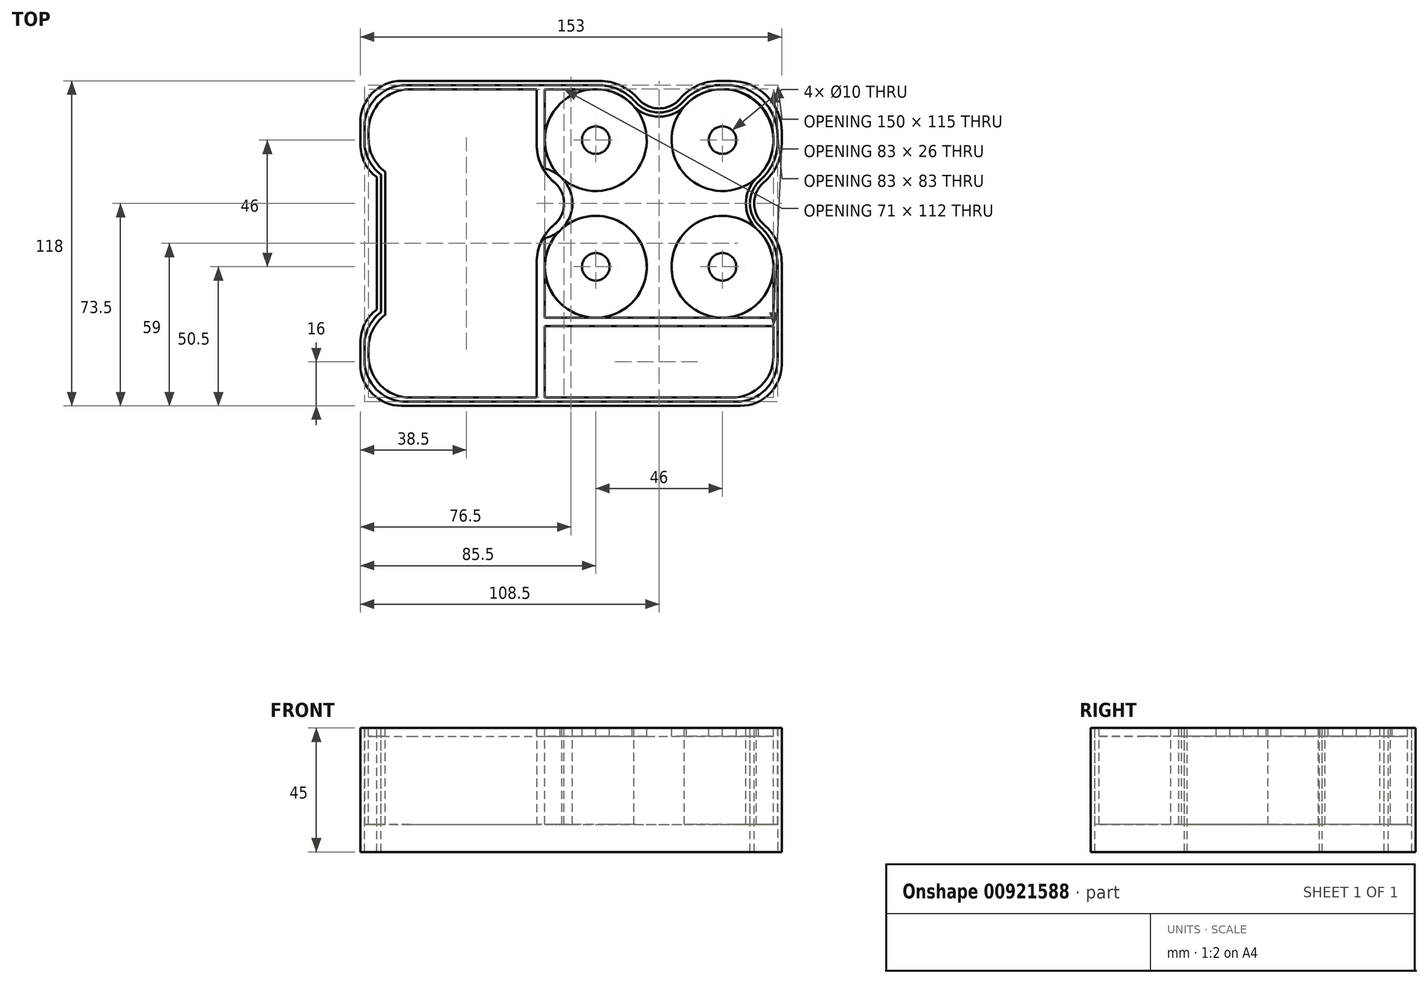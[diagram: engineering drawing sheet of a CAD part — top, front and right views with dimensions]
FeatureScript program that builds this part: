
annotation { "Feature Type Name" : "Feature", "Feature Type Description" : "" }
export const myFeature = defineFeature(function(context is Context, id is Id, definition is map)
    precondition{}
    {
        {
            var Q0;
            Q0=qCreatedBy(makeId("Top.planeOp"),FACE);
            var sketch = newSketch(context, id + "F0", { "sketchPlane" : qUnion([Q0])});
            skLineSegment(sketch, "E0.bottom", {"start": v(-44.5, 44.5) * mm, "end": v(-10, 44.5) * mm});
            skLineSegment(sketch, "E0.top", {"start": v(-44.5, -44.5) * mm, "end": v(41.5, -44.5) * mm});
            skLineSegment(sketch, "E0.left", {"start": v(-44.5, 41.5) * mm, "end": v(-44.5, 10) * mm});
            skLineSegment(sketch, "E0.right", {"start": v(44.5, 44.5) * mm, "end": v(44.5, 10) * mm});
            skPoint(sketch, "E0.middle", {"position": v(0, 0) * mm});
            skArc(sketch, "E1", {"start": v(-44.5, -10) * mm, "mid": v(-34.5, 0) * mm, "end": v(-44.5, 10) * mm});
            skArc(sketch, "E2", {"start": v(44.5, 10) * mm, "mid": v(34.5, 0) * mm, "end": v(44.5, -10) * mm});
            skArc(sketch, "E3", {"start": v(-10, 44.5) * mm, "mid": v(0, 34.5) * mm, "end": v(10, 44.5) * mm});
            skLineSegment(sketch, "E4.trimOffspring", {"start": v(10, 44.5) * mm, "end": v(44.5, 44.5) * mm});
            skLineSegment(sketch, "E5.trimOffspring", {"start": v(44.5, -10) * mm, "end": v(44.5, -44.5) * mm});
            skLineSegment(sketch, "E6.trimOffspring", {"start": v(-44.5, -10) * mm, "end": v(-44.5, -44.5) * mm});
            skLineSegment(sketch, "E7.bottom", {"start": v(-43, 43) * mm, "end": v(-11.4, 43) * mm});
            skLineSegment(sketch, "E7.top", {"start": v(-43, -43) * mm, "end": v(41.5, -43) * mm});
            skLineSegment(sketch, "E7.left", {"start": v(-43, 41.5) * mm, "end": v(-43, 11.4) * mm});
            skLineSegment(sketch, "E7.right", {"start": v(43, 43) * mm, "end": v(43, 11.4) * mm});
            skArc(sketch, "E8", {"start": v(-43, -11.4) * mm, "mid": v(-33, 0) * mm, "end": v(-43, 11.4) * mm});
            skArc(sketch, "E9", {"start": v(43, 11.4) * mm, "mid": v(33, 0) * mm, "end": v(43, -11.4) * mm});
            skArc(sketch, "E10", {"start": v(-11.4, 43) * mm, "mid": v(0, 33) * mm, "end": v(11.4, 43) * mm});
            skLineSegment(sketch, "E11.trimOffspring", {"start": v(-43, -11.4) * mm, "end": v(-43, -43) * mm});
            skLineSegment(sketch, "E12.trimOffspring", {"start": v(11.4, 43) * mm, "end": v(43, 43) * mm});
            skLineSegment(sketch, "E13.trimOffspring", {"start": v(43, -11.4) * mm, "end": v(43, -43) * mm});
            skLineSegment(sketch, "E14.bottom", {"start": v(-41.5, 41.5) * mm, "end": v(-12.65, 41.5) * mm});
            skLineSegment(sketch, "E14.top", {"start": v(-41.5, -41.5) * mm, "end": v(41.5, -41.5) * mm});
            skLineSegment(sketch, "E14.left", {"start": v(-41.5, 41.5) * mm, "end": v(-41.5, 12.65) * mm});
            skLineSegment(sketch, "E14.right", {"start": v(41.5, 41.5) * mm, "end": v(41.5, 12.65) * mm});
            skArc(sketch, "E15", {"start": v(-41.5, -12.65) * mm, "mid": v(-31.5, 0) * mm, "end": v(-41.5, 12.65) * mm});
            skArc(sketch, "E16", {"start": v(41.5, 12.65) * mm, "mid": v(31.5, 0) * mm, "end": v(41.5, -12.65) * mm});
            skArc(sketch, "E17", {"start": v(-12.65, 41.5) * mm, "mid": v(0, 31.5) * mm, "end": v(12.65, 41.5) * mm});
            skLineSegment(sketch, "E18.trimOffspring", {"start": v(12.65, 41.5) * mm, "end": v(41.5, 41.5) * mm});
            skLineSegment(sketch, "E19.trimOffspring", {"start": v(41.5, -12.65) * mm, "end": v(41.5, -41.5) * mm});
            skLineSegment(sketch, "E20.trimOffspring", {"start": v(-41.5, -12.65) * mm, "end": v(-41.5, -41.5) * mm});
            skLineSegment(sketch, "E21.bottom", {"start": v(-23, 23) * mm, "end": v(23, 23) * mm, "construction": true});
            skLineSegment(sketch, "E21.top", {"start": v(-23, -23) * mm, "end": v(23, -23) * mm, "construction": true});
            skLineSegment(sketch, "E21.left", {"start": v(-23, 23) * mm, "end": v(-23, -23) * mm, "construction": true});
            skLineSegment(sketch, "E21.right", {"start": v(23, 23) * mm, "end": v(23, -23) * mm, "construction": true});
            skCircle(sketch, "E22", {"center": v(-23, 23) * mm, "radius": 18.5 * mm});
            skCircle(sketch, "E23", {"center": v(23, 23) * mm, "radius": 18.5 * mm});
            skCircle(sketch, "E24", {"center": v(23, -23) * mm, "radius": 18.5 * mm});
            skCircle(sketch, "E25", {"center": v(-23, -23) * mm, "radius": 18.5 * mm});
            skLineSegment(sketch, "E26.top", {"start": v(44.5, -73.5) * mm, "end": v(-44.5, -73.5) * mm});
            skLineSegment(sketch, "E26.left", {"start": v(44.5, -44.5) * mm, "end": v(44.5, -73.5) * mm});
            skLineSegment(sketch, "E26.right", {"start": v(-44.5, -44.5) * mm, "end": v(-44.5, -73.5) * mm});
            skPoint(sketch, "E26.middle", {"position": v(0, -59) * mm});
            skLineSegment(sketch, "E27.bottom", {"start": v(-43, -72) * mm, "end": v(43, -72) * mm});
            skLineSegment(sketch, "E27.left", {"start": v(-43, -70.5) * mm, "end": v(-43, -46) * mm});
            skLineSegment(sketch, "E27.right", {"start": v(43, -72) * mm, "end": v(43, -46) * mm});
            skLineSegment(sketch, "E28.top", {"start": v(-41.5, -70.5) * mm, "end": v(41.5, -70.5) * mm});
            skLineSegment(sketch, "E28.left", {"start": v(-41.5, -47.5) * mm, "end": v(-41.5, -70.5) * mm});
            skLineSegment(sketch, "E28.right", {"start": v(41.5, -47.5) * mm, "end": v(41.5, -70.5) * mm});
            skLineSegment(sketch, "E29.bottom", {"start": v(-44.5, -73.5) * mm, "end": v(-108.5, -73.5) * mm});
            skLineSegment(sketch, "E29.top", {"start": v(-44, 44.5) * mm, "end": v(-108.5, 44.5) * mm});
            skLineSegment(sketch, "E29.left", {"start": v(-44.5, -73.5) * mm, "end": v(-44.5, 41.5) * mm});
            skLineSegment(sketch, "E29.right", {"start": v(-108.5, -73.5) * mm, "end": v(-108.5, -38.5) * mm});
            skLineSegment(sketch, "E30", {"start": v(-108.5, -14.5) * mm, "end": v(-44.5, -14.5) * mm, "construction": true});
            skPoint(sketch, "E31", {"position": v(-76.5, -14.5) * mm});
            skLineSegment(sketch, "E32.bottom", {"start": v(-107, 43) * mm, "end": v(-46, 43) * mm});
            skLineSegment(sketch, "E32.top", {"start": v(-107, -72) * mm, "end": v(-46, -72) * mm});
            skLineSegment(sketch, "E32.left", {"start": v(-107, 43) * mm, "end": v(-107, 10.5) * mm});
            skLineSegment(sketch, "E32.right", {"start": v(-46, 41.5) * mm, "end": v(-46, -70.5) * mm});
            skLineSegment(sketch, "E33.bottom", {"start": v(-105.5, 41.5) * mm, "end": v(-47.5, 41.5) * mm});
            skLineSegment(sketch, "E33.top", {"start": v(-105.5, -70.5) * mm, "end": v(-47.5, -70.5) * mm});
            skLineSegment(sketch, "E33.left", {"start": v(-105.5, 41.5) * mm, "end": v(-105.5, 11.5) * mm});
            skLineSegment(sketch, "E33.right", {"start": v(-47.5, 41.5) * mm, "end": v(-47.5, -70.5) * mm});
            skLineSegment(sketch, "E34", {"start": v(41.5, -41.5) * mm, "end": v(41.5, -47.5) * mm});
            skLineSegment(sketch, "E35", {"start": v(43, -43) * mm, "end": v(43, -46) * mm});
            skLineSegment(sketch, "E36.trimOffspring", {"start": v(41.5, -44.5) * mm, "end": v(-44.5, -44.5) * mm});
            skLineSegment(sketch, "E37", {"start": v(-47.5, -70.5) * mm, "end": v(-41.5, -70.5) * mm});
            skLineSegment(sketch, "E38", {"start": v(-46, -72) * mm, "end": v(-43, -72) * mm});
            skLineSegment(sketch, "E39", {"start": v(-46, 43) * mm, "end": v(-43, 43) * mm});
            skLineSegment(sketch, "E40", {"start": v(-47.5, 41.5) * mm, "end": v(-41.5, 41.5) * mm});
            skLineSegment(sketch, "E41", {"start": v(-43, -46) * mm, "end": v(-43, -44.5) * mm});
            skLineSegment(sketch, "E42", {"start": v(-41.5, -47.5) * mm, "end": v(-41.5, -45) * mm});
            skLineSegment(sketch, "E43", {"start": v(-41.5, -45) * mm, "end": v(-41.5, -44.5) * mm});
            skCircle(sketch, "E44", {"center": v(-23, 23) * mm, "radius": 5 * mm});
            skCircle(sketch, "E45", {"center": v(23, 23) * mm, "radius": 5 * mm});
            skCircle(sketch, "E46", {"center": v(-23, -23) * mm, "radius": 5 * mm});
            skCircle(sketch, "E47", {"center": v(23, -23) * mm, "radius": 5 * mm});
            skLineSegment(sketch, "E48", {"start": v(-102.5, 9.5) * mm, "end": v(-102.5, -37.89) * mm});
            skLineSegment(sketch, "E49", {"start": v(-101, -37.89) * mm, "end": v(-101, 10.5) * mm});
            skLineSegment(sketch, "E50", {"start": v(-99.5, -37.89) * mm, "end": v(-99.5, 9.5) * mm});
            skLineSegment(sketch, "E51", {"start": v(-102.5, 9.5) * mm, "end": v(-108.5, 9.5) * mm});
            skLineSegment(sketch, "E52", {"start": v(-107, 10.5) * mm, "end": v(-101, 10.5) * mm});
            skLineSegment(sketch, "E53", {"start": v(-99.5, 9.5) * mm, "end": v(-99.5, 10.5) * mm});
            skLineSegment(sketch, "E54", {"start": v(-105.5, 11.5) * mm, "end": v(-99.5, 11.5) * mm});
            skLineSegment(sketch, "E55", {"start": v(-99.5, 11.5) * mm, "end": v(-99.5, 10.5) * mm});
            skLineSegment(sketch, "E56", {"start": v(-108.5, -38.5) * mm, "end": v(-102.5, -38.5) * mm});
            skLineSegment(sketch, "E57", {"start": v(-102.5, -38.5) * mm, "end": v(-102.5, -37.89) * mm});
            skLineSegment(sketch, "E58", {"start": v(-107, -39.5) * mm, "end": v(-101, -39.5) * mm});
            skLineSegment(sketch, "E59", {"start": v(-101, -39.5) * mm, "end": v(-101, -37.89) * mm});
            skLineSegment(sketch, "E60", {"start": v(-105.5, -40.5) * mm, "end": v(-99.5, -40.5) * mm});
            skLineSegment(sketch, "E61", {"start": v(-99.5, -40.5) * mm, "end": v(-99.5, -37.89) * mm});
            skLineSegment(sketch, "E62.trimOffspring", {"start": v(-107, -39.5) * mm, "end": v(-107, -72) * mm});
            skLineSegment(sketch, "E63.trimOffspring", {"start": v(-105.5, -40.5) * mm, "end": v(-105.5, -70.5) * mm});
            skLineSegment(sketch, "E64.trimOffspring", {"start": v(-108.5, 9.5) * mm, "end": v(-108.5, 44.5) * mm});
            skSolve(sketch);
        }
        {
            var Q0;
            Q0=makeQuery(id+"F0.imprint","IMPRINT",FACE,{"disambiguationData":[TD([[makeQuery(id+"F0.imprint","IMPRINT",EDGE,{"derivedFrom":sQuery(id+"F0.wireOp",EDGE,"E14.bottom")}),-1.0]])]});
            var Q1;
            {var subQ5=sQuery(id+"F0.wireOp",EDGE,"E15");Q1=makeQuery(id+"F0.imprint","IMPRINT",FACE,{"disambiguationData":[TD([[makeQuery(id+"F0.imprint","IMPRINT",EDGE,{"derivedFrom":subQ5}),-1.0]])]});}
            var Q2;
            {var subQ0=sQuery(id+"F0.wireOp",EDGE,"E20.trimOffspring");var subQ1=sQuery(id+"F0.wireOp",EDGE,"E14.top");var subQ2=makeQuery(id+"F0.imprint","INTERSECT",VERTEX,{"derivedFrom":[subQ1,subQ0]});Q2=makeQuery(id+"F0.imprint","IMPRINT",FACE,{"disambiguationData":[TD([[makeQuery(id+"F0.imprint","IMPRINT",EDGE,{"disambiguationData":[TD([[subQ2,-1.0]])],"derivedFrom":subQ1}),1.0]])]});}
            var Q3;
            {var subQ0=sQuery(id+"F0.wireOp",EDGE,"E25");var subQ1=sQuery(id+"F0.wireOp",EDGE,"E14.top");var subQ2=makeQuery(id+"F0.imprint","INTERSECT",VERTEX,{"derivedFrom":[subQ1,subQ0]});Q3=makeQuery(id+"F0.imprint","IMPRINT",FACE,{"disambiguationData":[TD([[makeQuery(id+"F0.imprint","IMPRINT",EDGE,{"disambiguationData":[TD([[subQ2,-1.0]])],"derivedFrom":subQ1}),1.0]])]});}
            var Q4;
            {var subQ0=sQuery(id+"F0.wireOp",EDGE,"E19.trimOffspring");var subQ1=sQuery(id+"F0.wireOp",EDGE,"E14.top");var subQ2=makeQuery(id+"F0.imprint","INTERSECT",VERTEX,{"derivedFrom":[subQ1,subQ0]});Q4=makeQuery(id+"F0.imprint","IMPRINT",FACE,{"disambiguationData":[TD([[makeQuery(id+"F0.imprint","IMPRINT",EDGE,{"disambiguationData":[TD([[subQ2,1.0]])],"derivedFrom":subQ1}),1.0]])]});}
            var Q5;
            {var subQ1=sQuery(id+"F0.wireOp",EDGE,"E16");Q5=makeQuery(id+"F0.imprint","IMPRINT",FACE,{"disambiguationData":[TD([[makeQuery(id+"F0.imprint","IMPRINT",EDGE,{"derivedFrom":subQ1}),-1.0]])]});}
            var Q6;
            {var subQ0=sQuery(id+"F0.wireOp",EDGE,"E18.trimOffspring");var subQ1=sQuery(id+"F0.wireOp",EDGE,"E14.right");var subQ2=makeQuery(id+"F0.imprint","INTERSECT",VERTEX,{"derivedFrom":[subQ1,subQ0]});Q6=makeQuery(id+"F0.imprint","IMPRINT",FACE,{"disambiguationData":[TD([[makeQuery(id+"F0.imprint","IMPRINT",EDGE,{"disambiguationData":[TD([[subQ2,-1.0]])],"derivedFrom":subQ1}),-1.0]])]});}
            var Q7;
            {var subQ8=sQuery(id+"F0.wireOp",EDGE,"E17");Q7=makeQuery(id+"F0.imprint","IMPRINT",FACE,{"disambiguationData":[TD([[makeQuery(id+"F0.imprint","IMPRINT",EDGE,{"derivedFrom":subQ8}),-1.0]])]});}
            var Q8;
            {var subQ7=sQuery(id+"F0.wireOp",EDGE,"E22");var subQ12=sQuery(id+"F0.wireOp",EDGE,"E21.bottom");var subQ15=makeQuery(id+"F0.imprint","INTERSECT",VERTEX,{"derivedFrom":[subQ12,subQ7]});Q8=makeQuery(id+"F0.imprint","IMPRINT",FACE,{"disambiguationData":[TD([[makeQuery(id+"F0.imprint","IMPRINT",EDGE,{"disambiguationData":[TD([[subQ15,-1.0]])],"derivedFrom":subQ12}),-1.0]])]});}
            var Q9;
            Q9=makeQuery(id+"F0.imprint","IMPRINT",FACE,{"disambiguationData":[TD([[makeQuery(id+"F0.imprint","IMPRINT",EDGE,{"derivedFrom":sQuery(id+"F0.wireOp",EDGE,"E33.bottom")}),-1.0]])]});
            var Q10;
            Q10=makeQuery(id+"F0.imprint","IMPRINT",FACE,{"disambiguationData":[TD([[makeQuery(id+"F0.imprint","IMPRINT",EDGE,{"derivedFrom":sQuery(id+"F0.wireOp",EDGE,"E28.bottom")}),-1.0]])]});
            var Q11;
            {var subQ0=sQuery(id+"F0.wireOp",EDGE,"E32.right");Q11=makeQuery(id+"F0.imprint","IMPRINT",FACE,{"disambiguationData":[TD([[makeQuery(id+"F0.imprint","IMPRINT",EDGE,{"derivedFrom":subQ0}),-1.0]])]});}
            var Q12;
            {var subQ0=sQuery(id+"F0.wireOp",EDGE,"E1");Q12=makeQuery(id+"F0.imprint","IMPRINT",FACE,{"disambiguationData":[TD([[makeQuery(id+"F0.imprint","IMPRINT",EDGE,{"derivedFrom":subQ0}),1.0]])]});}
            var Q13;
            {var subQ9=sQuery(id+"F0.wireOp",EDGE,"E32.right");Q13=makeQuery(id+"F0.imprint","IMPRINT",FACE,{"disambiguationData":[TD([[makeQuery(id+"F0.imprint","IMPRINT",EDGE,{"derivedFrom":subQ9}),1.0]])]});}
            var Q14;
            Q14=makeQuery(id+"F0.imprint","IMPRINT",FACE,{"disambiguationData":[TD([[makeQuery(id+"F0.imprint","IMPRINT",EDGE,{"derivedFrom":sQuery(id+"F0.wireOp",EDGE,"E28.top")}),1.0]])]});
            extrude(context, id + "F1", {"entities" : qUnion([Q0, Q1, Q2, Q3, Q4, Q5, Q6, Q7, Q8, Q9, Q10, Q11, Q12, Q13, Q14]), "oppositeDirection" : true, "depth" : 3 * mm, "offsetDistance" : 25 * mm});
        }
        {
            var Q0;
            Q0=makeQuery(id+"F0.imprint","IMPRINT",FACE,{"disambiguationData":[TD([[makeQuery(id+"F0.imprint","IMPRINT",EDGE,{"derivedFrom":sQuery(id+"F0.wireOp",EDGE,"E0.bottom")}),-1.0]])]});
            extrude(context, id + "F2", {"entities" : qUnion([Q0]), "oppositeDirection" : true, "depth" : 45 * mm, "offsetDistance" : 25 * mm});
        }
        {
            var Q0;
            Q0=makeQuery(id+"F0.imprint","IMPRINT",FACE,{"disambiguationData":[TD([[makeQuery(id+"F0.imprint","IMPRINT",EDGE,{"derivedFrom":sQuery(id+"F0.wireOp",EDGE,"E7.bottom")}),-1.0]])]});
            var Q1;
            {var subQ9=sQuery(id+"F0.wireOp",EDGE,"E32.top");Q1=makeQuery(id+"F0.imprint","IMPRINT",FACE,{"disambiguationData":[TD([[makeQuery(id+"F0.imprint","IMPRINT",EDGE,{"derivedFrom":subQ9}),1.0]])]});}
            var Q2;
            {var subQ5=sQuery(id+"F0.wireOp",EDGE,"E1");Q2=makeQuery(id+"F0.imprint","IMPRINT",FACE,{"disambiguationData":[TD([[makeQuery(id+"F0.imprint","IMPRINT",EDGE,{"derivedFrom":subQ5}),-1.0]])]});}
            var Q3;
            {var subQ7=sQuery(id+"F0.wireOp",EDGE,"E7.top");Q3=makeQuery(id+"F0.imprint","IMPRINT",FACE,{"disambiguationData":[TD([[makeQuery(id+"F0.imprint","IMPRINT",EDGE,{"derivedFrom":subQ7}),1.0]])]});}
            var Q4;
            {var subQ6=sQuery(id+"F0.wireOp",EDGE,"E27.left");Q4=makeQuery(id+"F0.imprint","IMPRINT",FACE,{"disambiguationData":[TD([[makeQuery(id+"F0.imprint","IMPRINT",EDGE,{"derivedFrom":subQ6}),1.0]])]});}
            var Q5;
            {var subQ1=sQuery(id+"F0.wireOp",EDGE,"E27.left");Q5=makeQuery(id+"F0.imprint","IMPRINT",FACE,{"disambiguationData":[TD([[makeQuery(id+"F0.imprint","IMPRINT",EDGE,{"derivedFrom":subQ1}),-1.0]])]});}
            extrude(context, id + "F3", {"entities" : qUnion([Q0, Q1, Q2, Q3, Q4, Q5]), "oppositeDirection" : true, "depth" : 35 * mm, "offsetDistance" : 25 * mm});
        }
        {
            var Q0;
            Q0=makeQuery(id+"F0.imprint","IMPRINT",FACE,{"disambiguationData":[TD([[makeQuery(id+"F0.imprint","IMPRINT",EDGE,{"derivedFrom":sQuery(id+"F0.wireOp",EDGE,"E44")}),1.0]])]});
            var Q1;
            Q1=makeQuery(id+"F0.imprint","IMPRINT",FACE,{"disambiguationData":[TD([[makeQuery(id+"F0.imprint","IMPRINT",EDGE,{"derivedFrom":sQuery(id+"F0.wireOp",EDGE,"E45")}),1.0]])]});
            var Q2;
            Q2=makeQuery(id+"F0.imprint","IMPRINT",FACE,{"disambiguationData":[TD([[makeQuery(id+"F0.imprint","IMPRINT",EDGE,{"derivedFrom":sQuery(id+"F0.wireOp",EDGE,"E47")}),1.0]])]});
            var Q3;
            Q3=makeQuery(id+"F0.imprint","IMPRINT",FACE,{"disambiguationData":[TD([[makeQuery(id+"F0.imprint","IMPRINT",EDGE,{"derivedFrom":sQuery(id+"F0.wireOp",EDGE,"E46")}),1.0]])]});
            extrude(context, id + "F4", {"entities" : qUnion([Q0, Q1, Q2, Q3]), "oppositeDirection" : true, "depth" : 3 * mm, "offsetDistance" : 25 * mm});
        }
        {
            var Q0;
            Q0=makeQuery(id+"F0.imprint","IMPRINT",FACE,{"disambiguationData":[TD([[makeQuery(id+"F0.imprint","IMPRINT",EDGE,{"derivedFrom":sQuery(id+"F0.wireOp",EDGE,"E44")}),-1.0]])]});
            var Q1;
            Q1=makeQuery(id+"F0.imprint","IMPRINT",FACE,{"disambiguationData":[TD([[makeQuery(id+"F0.imprint","IMPRINT",EDGE,{"derivedFrom":sQuery(id+"F0.wireOp",EDGE,"E45")}),-1.0]])]});
            var Q2;
            Q2=makeQuery(id+"F0.imprint","IMPRINT",FACE,{"disambiguationData":[TD([[makeQuery(id+"F0.imprint","IMPRINT",EDGE,{"derivedFrom":sQuery(id+"F0.wireOp",EDGE,"E46")}),-1.0]])]});
            var Q3;
            Q3=makeQuery(id+"F0.imprint","IMPRINT",FACE,{"disambiguationData":[TD([[makeQuery(id+"F0.imprint","IMPRINT",EDGE,{"derivedFrom":sQuery(id+"F0.wireOp",EDGE,"E47")}),-1.0]])]});
            extrude(context, id + "F5", {"entities" : qUnion([Q0, Q1, Q2, Q3]), "oppositeDirection" : true, "depth" : 3 * mm, "offsetDistance" : 25 * mm});
        }
        {
            var Q0;
            Q0=makeQuery(id+"F2.opExtrude","SWEPT_EDGE",EDGE,{"disambiguationData":[OSD([sQuery(id+"F0.wireOp",EDGE,"E0.right"),sQuery(id+"F0.wireOp",EDGE,"E4.trimOffspring")])]});
            var Q1;
            Q1=makeQuery(id+"F2.opExtrude","SWEPT_EDGE",EDGE,{"disambiguationData":[OSD([sQuery(id+"F0.wireOp",EDGE,"E7.right"),sQuery(id+"F0.wireOp",EDGE,"E12.trimOffspring")])]});
            var Q2;
            Q2=makeQuery(id+"F2.opExtrude","SWEPT_EDGE",EDGE,{"disambiguationData":[OSD([sQuery(id+"F0.wireOp",EDGE,"E0.right"),sQuery(id+"F0.wireOp",EDGE,"E2")])]});
            var Q3;
            Q3=makeQuery(id+"F2.opExtrude","SWEPT_EDGE",EDGE,{"disambiguationData":[OSD([sQuery(id+"F0.wireOp",EDGE,"E7.right"),sQuery(id+"F0.wireOp",EDGE,"E9")])]});
            var Q4;
            Q4=makeQuery(id+"F2.opExtrude","SWEPT_EDGE",EDGE,{"disambiguationData":[OSD([sQuery(id+"F0.wireOp",EDGE,"E3"),sQuery(id+"F0.wireOp",EDGE,"E4.trimOffspring")])]});
            var Q5;
            Q5=makeQuery(id+"F2.opExtrude","SWEPT_EDGE",EDGE,{"disambiguationData":[OSD([sQuery(id+"F0.wireOp",EDGE,"E10"),sQuery(id+"F0.wireOp",EDGE,"E12.trimOffspring")])]});
            var Q6;
            Q6=makeQuery(id+"F2.opExtrude","SWEPT_EDGE",EDGE,{"disambiguationData":[OSD([sQuery(id+"F0.wireOp",EDGE,"E0.bottom"),sQuery(id+"F0.wireOp",EDGE,"E3")])]});
            var Q7;
            Q7=makeQuery(id+"F2.opExtrude","SWEPT_EDGE",EDGE,{"disambiguationData":[OSD([sQuery(id+"F0.wireOp",EDGE,"E7.bottom"),sQuery(id+"F0.wireOp",EDGE,"E10")])]});
            var Q8;
            Q8=makeQuery(id+"F2.opExtrude","SWEPT_EDGE",EDGE,{"disambiguationData":[OSD([sQuery(id+"F0.wireOp",EDGE,"E2"),sQuery(id+"F0.wireOp",EDGE,"E5.trimOffspring")])]});
            var Q9;
            Q9=makeQuery(id+"F2.opExtrude","SWEPT_EDGE",EDGE,{"disambiguationData":[OSD([sQuery(id+"F0.wireOp",EDGE,"E9"),sQuery(id+"F0.wireOp",EDGE,"E13.trimOffspring")])]});
            var Q10;
            {var subQ0=sQuery(id+"F0.wireOp",EDGE,"E29.left");var subQ1=sQuery(id+"F0.wireOp",EDGE,"E1");Q10=makeQuery(id+"FE6vsyq0CEjp5Nf_9.opExtrude","SWEPT_EDGE",EDGE,{"disambiguationData":[OSD([subQ1,subQ0]),TDD([makeQuery(id+"F0.imprint","INTERSECT",VERTEX,{"disambiguationData":[OD(1.0)],"derivedFrom":[subQ1,subQ0]})])]});}
            var Q11;
            Q11=makeQuery(id+"FE6vsyq0CEjp5Nf_9.opExtrude","SWEPT_EDGE",EDGE,{"disambiguationData":[OSD([sQuery(id+"F0.wireOp",EDGE,"E14.left"),sQuery(id+"F0.wireOp",EDGE,"E15")])]});
            var Q12;
            {var subQ0=sQuery(id+"F0.wireOp",EDGE,"E29.left");var subQ1=sQuery(id+"F0.wireOp",EDGE,"E1");Q12=makeQuery(id+"FE6vsyq0CEjp5Nf_9.opExtrude","SWEPT_EDGE",EDGE,{"disambiguationData":[OSD([subQ1,subQ0]),TDD([makeQuery(id+"F0.imprint","INTERSECT",VERTEX,{"disambiguationData":[OD(0.0)],"derivedFrom":[subQ1,subQ0]})])]});}
            var Q13;
            Q13=makeQuery(id+"FE6vsyq0CEjp5Nf_9.opExtrude","SWEPT_EDGE",EDGE,{"disambiguationData":[OSD([sQuery(id+"F0.wireOp",EDGE,"E15"),sQuery(id+"F0.wireOp",EDGE,"E20.trimOffspring")])]});
            fillet(context, id + "F6", {"entities" : qUnion([Q0, Q1, Q2, Q3, Q4, Q5, Q6, Q7, Q8, Q9, Q10, Q11, Q12, Q13]), "radius" : 18.5 * mm, "tangentPropagation" : true, "allowEdgeOverflow" : false});
        }
        {
            var Q0;
            Q0=makeQuery(id+"F1.opExtrude","SWEPT_EDGE",EDGE,{"disambiguationData":[OSD([sQuery(id+"F0.wireOp",EDGE,"E14.right"),sQuery(id+"F0.wireOp",EDGE,"E18.trimOffspring")])]});
            var Q1;
            Q1=makeQuery(id+"F1.opExtrude","SWEPT_EDGE",EDGE,{"disambiguationData":[OSD([sQuery(id+"F0.wireOp",EDGE,"E17"),sQuery(id+"F0.wireOp",EDGE,"E18.trimOffspring")])]});
            var Q2;
            Q2=makeQuery(id+"F1.opExtrude","SWEPT_EDGE",EDGE,{"disambiguationData":[OSD([sQuery(id+"F0.wireOp",EDGE,"E14.bottom"),sQuery(id+"F0.wireOp",EDGE,"E17")])]});
            var Q3;
            Q3=makeQuery(id+"F1.opExtrude","SWEPT_EDGE",EDGE,{"disambiguationData":[OSD([sQuery(id+"F0.wireOp",EDGE,"E14.right"),sQuery(id+"F0.wireOp",EDGE,"E16")])]});
            var Q4;
            Q4=makeQuery(id+"F1.opExtrude","SWEPT_EDGE",EDGE,{"disambiguationData":[OSD([sQuery(id+"F0.wireOp",EDGE,"E16"),sQuery(id+"F0.wireOp",EDGE,"E19.trimOffspring")])]});
            var Q5;
            {var subQ0=sQuery(id+"F0.wireOp",EDGE,"E29.left");var subQ1=sQuery(id+"F0.wireOp",EDGE,"E1");Q5=makeQuery(id+"F1.opExtrude","SWEPT_EDGE",EDGE,{"disambiguationData":[OSD([subQ1,subQ0]),TDD([makeQuery(id+"F0.imprint","INTERSECT",VERTEX,{"disambiguationData":[OD(1.0)],"derivedFrom":[subQ1,subQ0]})])]});}
            var Q6;
            {var subQ0=sQuery(id+"F0.wireOp",EDGE,"E29.left");var subQ1=sQuery(id+"F0.wireOp",EDGE,"E1");Q6=makeQuery(id+"F1.opExtrude","SWEPT_EDGE",EDGE,{"disambiguationData":[OSD([subQ1,subQ0]),TDD([makeQuery(id+"F0.imprint","INTERSECT",VERTEX,{"disambiguationData":[OD(0.0)],"derivedFrom":[subQ1,subQ0]})])]});}
            fillet(context, id + "F7", {"entities" : qUnion([Q0, Q1, Q2, Q3, Q4, Q5, Q6]), "radius" : 18 * mm, "tangentPropagation" : true, "allowEdgeOverflow" : false});
        }
        {
            var Q0;
            Q0=makeQuery(id+"F3.opExtrude","SWEPT_EDGE",EDGE,{"disambiguationData":[OSD([sQuery(id+"F0.wireOp",EDGE,"E7.bottom"),sQuery(id+"F0.wireOp",EDGE,"E10")])]});
            var Q1;
            Q1=makeQuery(id+"F3.opExtrude","SWEPT_EDGE",EDGE,{"disambiguationData":[OSD([sQuery(id+"F0.wireOp",EDGE,"E14.bottom"),sQuery(id+"F0.wireOp",EDGE,"E17")])]});
            var Q2;
            Q2=makeQuery(id+"F3.opExtrude","SWEPT_EDGE",EDGE,{"disambiguationData":[OSD([sQuery(id+"F0.wireOp",EDGE,"E10"),sQuery(id+"F0.wireOp",EDGE,"E12.trimOffspring")])]});
            var Q3;
            Q3=makeQuery(id+"F3.opExtrude","SWEPT_EDGE",EDGE,{"disambiguationData":[OSD([sQuery(id+"F0.wireOp",EDGE,"E17"),sQuery(id+"F0.wireOp",EDGE,"E18.trimOffspring")])]});
            var Q4;
            Q4=makeQuery(id+"F3.opExtrude","SWEPT_EDGE",EDGE,{"disambiguationData":[OSD([sQuery(id+"F0.wireOp",EDGE,"E7.right"),sQuery(id+"F0.wireOp",EDGE,"E12.trimOffspring")])]});
            var Q5;
            Q5=makeQuery(id+"F3.opExtrude","SWEPT_EDGE",EDGE,{"disambiguationData":[OSD([sQuery(id+"F0.wireOp",EDGE,"E14.right"),sQuery(id+"F0.wireOp",EDGE,"E18.trimOffspring")])]});
            var Q6;
            Q6=makeQuery(id+"F3.opExtrude","SWEPT_EDGE",EDGE,{"disambiguationData":[OSD([sQuery(id+"F0.wireOp",EDGE,"E7.right"),sQuery(id+"F0.wireOp",EDGE,"E9")])]});
            var Q7;
            Q7=makeQuery(id+"F3.opExtrude","SWEPT_EDGE",EDGE,{"disambiguationData":[OSD([sQuery(id+"F0.wireOp",EDGE,"E14.right"),sQuery(id+"F0.wireOp",EDGE,"E16")])]});
            var Q8;
            Q8=makeQuery(id+"F3.opExtrude","SWEPT_EDGE",EDGE,{"disambiguationData":[OSD([sQuery(id+"F0.wireOp",EDGE,"E9"),sQuery(id+"F0.wireOp",EDGE,"E13.trimOffspring")])]});
            var Q9;
            Q9=makeQuery(id+"F3.opExtrude","SWEPT_EDGE",EDGE,{"disambiguationData":[OSD([sQuery(id+"F0.wireOp",EDGE,"E16"),sQuery(id+"F0.wireOp",EDGE,"E19.trimOffspring")])]});
            var Q10;
            Q10=makeQuery(id+"FE6vsyq0CEjp5Nf_9.opExtrude","SWEPT_EDGE",EDGE,{"disambiguationData":[OSD([sQuery(id+"F0.wireOp",EDGE,"E14.top"),sQuery(id+"F0.wireOp",EDGE,"E20.trimOffspring")])]});
            var Q11;
            Q11=makeQuery(id+"F3.opExtrude","SWEPT_EDGE",EDGE,{"disambiguationData":[OSD([sQuery(id+"F0.wireOp",EDGE,"E14.bottom"),sQuery(id+"F0.wireOp",EDGE,"E14.left"),sQuery(id+"F0.wireOp",EDGE,"E40")])]});
            var Q12;
            Q12=makeQuery(id+"F3.opExtrude","SWEPT_EDGE",EDGE,{"disambiguationData":[OSD([sQuery(id+"F0.wireOp",EDGE,"E14.top"),sQuery(id+"F0.wireOp",EDGE,"E20.trimOffspring")])]});
            var Q13;
            Q13=makeQuery(id+"F3.opExtrude","SWEPT_EDGE",EDGE,{"disambiguationData":[OSD([sQuery(id+"F0.wireOp",EDGE,"E14.top"),sQuery(id+"F0.wireOp",EDGE,"E19.trimOffspring"),sQuery(id+"F0.wireOp",EDGE,"E34")])]});
            var Q14;
            {var subQ0=sQuery(id+"F0.wireOp",EDGE,"E29.left");var subQ1=sQuery(id+"F0.wireOp",EDGE,"E1");Q14=makeQuery(id+"F3.opExtrude","SWEPT_EDGE",EDGE,{"disambiguationData":[OSD([subQ1,subQ0]),TDD([makeQuery(id+"F0.imprint","INTERSECT",VERTEX,{"disambiguationData":[OD(0.0)],"derivedFrom":[subQ1,subQ0]})])]});}
            var Q15;
            Q15=makeQuery(id+"F3.opExtrude","SWEPT_EDGE",EDGE,{"disambiguationData":[OSD([sQuery(id+"F0.wireOp",EDGE,"E15"),sQuery(id+"F0.wireOp",EDGE,"E20.trimOffspring")])]});
            var Q16;
            {var subQ0=sQuery(id+"F0.wireOp",EDGE,"E29.left");var subQ1=sQuery(id+"F0.wireOp",EDGE,"E1");Q16=makeQuery(id+"F3.opExtrude","SWEPT_EDGE",EDGE,{"disambiguationData":[OSD([subQ1,subQ0]),TDD([makeQuery(id+"F0.imprint","INTERSECT",VERTEX,{"disambiguationData":[OD(1.0)],"derivedFrom":[subQ1,subQ0]})])]});}
            var Q17;
            Q17=makeQuery(id+"F3.opExtrude","SWEPT_EDGE",EDGE,{"disambiguationData":[OSD([sQuery(id+"F0.wireOp",EDGE,"E14.left"),sQuery(id+"F0.wireOp",EDGE,"E15")])]});
            fillet(context, id + "F8", {"entities" : qUnion([Q0, Q1, Q2, Q3, Q4, Q5, Q6, Q7, Q8, Q9, Q10, Q11, Q12, Q13, Q14, Q15, Q16, Q17]), "radius" : 18.5 * mm, "tangentPropagation" : true, "allowEdgeOverflow" : false});
        }
        {
            var Q0;
            Q0=makeQuery(id+"F2.opExtrude","SWEPT_EDGE",EDGE,{"disambiguationData":[OSD([sQuery(id+"F0.wireOp",EDGE,"E32.bottom"),sQuery(id+"F0.wireOp",EDGE,"E32.left")])]});
            var Q1;
            Q1=makeQuery(id+"F2.opExtrude","SWEPT_EDGE",EDGE,{"disambiguationData":[OSD([sQuery(id+"F0.wireOp",EDGE,"E32.left"),sQuery(id+"F0.wireOp",EDGE,"E52")])]});
            var Q2;
            Q2=makeQuery(id+"F2.opExtrude","SWEPT_EDGE",EDGE,{"disambiguationData":[OSD([sQuery(id+"F0.wireOp",EDGE,"E51"),sQuery(id+"F0.wireOp",EDGE,"E64.trimOffspring")])]});
            var Q3;
            Q3=makeQuery(id+"F2.opExtrude","SWEPT_EDGE",EDGE,{"disambiguationData":[OSD([sQuery(id+"F0.wireOp",EDGE,"E29.top"),sQuery(id+"F0.wireOp",EDGE,"E64.trimOffspring")])]});
            var Q4;
            Q4=makeQuery(id+"F2.opExtrude","SWEPT_EDGE",EDGE,{"disambiguationData":[OSD([sQuery(id+"F0.wireOp",EDGE,"E32.top"),sQuery(id+"F0.wireOp",EDGE,"E62.trimOffspring")])]});
            var Q5;
            Q5=makeQuery(id+"F2.opExtrude","SWEPT_EDGE",EDGE,{"disambiguationData":[OSD([sQuery(id+"F0.wireOp",EDGE,"E58"),sQuery(id+"F0.wireOp",EDGE,"E62.trimOffspring")])]});
            var Q6;
            Q6=makeQuery(id+"F2.opExtrude","SWEPT_EDGE",EDGE,{"disambiguationData":[OSD([sQuery(id+"F0.wireOp",EDGE,"E29.bottom"),sQuery(id+"F0.wireOp",EDGE,"E29.right")])]});
            var Q7;
            Q7=makeQuery(id+"F2.opExtrude","SWEPT_EDGE",EDGE,{"disambiguationData":[OSD([sQuery(id+"F0.wireOp",EDGE,"E29.right"),sQuery(id+"F0.wireOp",EDGE,"E56")])]});
            var Q8;
            Q8=makeQuery(id+"F2.opExtrude","SWEPT_EDGE",EDGE,{"disambiguationData":[OSD([sQuery(id+"F0.wireOp",EDGE,"E27.bottom"),sQuery(id+"F0.wireOp",EDGE,"E27.right")])]});
            var Q9;
            Q9=makeQuery(id+"F2.opExtrude","SWEPT_EDGE",EDGE,{"disambiguationData":[OSD([sQuery(id+"F0.wireOp",EDGE,"E26.top"),sQuery(id+"F0.wireOp",EDGE,"E26.left")])]});
            var Q10;
            Q10=makeQuery(id+"F3.opExtrude","SWEPT_EDGE",EDGE,{"disambiguationData":[OSD([sQuery(id+"F0.wireOp",EDGE,"E28.top"),sQuery(id+"F0.wireOp",EDGE,"E28.right")])]});
            var Q11;
            Q11=makeQuery(id+"F3.opExtrude","SWEPT_EDGE",EDGE,{"disambiguationData":[OSD([sQuery(id+"F0.wireOp",EDGE,"E27.bottom"),sQuery(id+"F0.wireOp",EDGE,"E27.right")])]});
            fillet(context, id + "F9", {"entities" : qUnion([Q0, Q1, Q2, Q3, Q4, Q5, Q6, Q7, Q8, Q9, Q10, Q11]), "radius" : 15 * mm, "tangentPropagation" : true, "allowEdgeOverflow" : false});
        }
        {
            var Q0;
            Q0=makeQuery(id+"F1.opExtrude","SWEPT_EDGE",EDGE,{"disambiguationData":[OSD([sQuery(id+"F0.wireOp",EDGE,"E33.bottom"),sQuery(id+"F0.wireOp",EDGE,"E33.left")])]});
            var Q1;
            Q1=makeQuery(id+"F1.opExtrude","SWEPT_EDGE",EDGE,{"disambiguationData":[OSD([sQuery(id+"F0.wireOp",EDGE,"E33.left"),sQuery(id+"F0.wireOp",EDGE,"E54")])]});
            var Q2;
            Q2=makeQuery(id+"F1.opExtrude","SWEPT_EDGE",EDGE,{"disambiguationData":[OSD([sQuery(id+"F0.wireOp",EDGE,"E60"),sQuery(id+"F0.wireOp",EDGE,"E63.trimOffspring")])]});
            var Q3;
            Q3=makeQuery(id+"F1.opExtrude","SWEPT_EDGE",EDGE,{"disambiguationData":[OSD([sQuery(id+"F0.wireOp",EDGE,"E33.top"),sQuery(id+"F0.wireOp",EDGE,"E63.trimOffspring")])]});
            var Q4;
            Q4=makeQuery(id+"F3.opExtrude","SWEPT_EDGE",EDGE,{"disambiguationData":[OSD([sQuery(id+"F0.wireOp",EDGE,"E33.bottom"),sQuery(id+"F0.wireOp",EDGE,"E33.left")])]});
            var Q5;
            Q5=makeQuery(id+"F3.opExtrude","SWEPT_EDGE",EDGE,{"disambiguationData":[OSD([sQuery(id+"F0.wireOp",EDGE,"E32.bottom"),sQuery(id+"F0.wireOp",EDGE,"E32.left")])]});
            var Q6;
            Q6=makeQuery(id+"F3.opExtrude","SWEPT_EDGE",EDGE,{"disambiguationData":[OSD([sQuery(id+"F0.wireOp",EDGE,"E33.left"),sQuery(id+"F0.wireOp",EDGE,"E54")])]});
            var Q7;
            Q7=makeQuery(id+"F3.opExtrude","SWEPT_EDGE",EDGE,{"disambiguationData":[OSD([sQuery(id+"F0.wireOp",EDGE,"E32.left"),sQuery(id+"F0.wireOp",EDGE,"E52")])]});
            var Q8;
            Q8=makeQuery(id+"F3.opExtrude","SWEPT_EDGE",EDGE,{"disambiguationData":[OSD([sQuery(id+"F0.wireOp",EDGE,"E60"),sQuery(id+"F0.wireOp",EDGE,"E63.trimOffspring")])]});
            var Q9;
            Q9=makeQuery(id+"F3.opExtrude","SWEPT_EDGE",EDGE,{"disambiguationData":[OSD([sQuery(id+"F0.wireOp",EDGE,"E58"),sQuery(id+"F0.wireOp",EDGE,"E62.trimOffspring")])]});
            var Q10;
            Q10=makeQuery(id+"F3.opExtrude","SWEPT_EDGE",EDGE,{"disambiguationData":[OSD([sQuery(id+"F0.wireOp",EDGE,"E33.top"),sQuery(id+"F0.wireOp",EDGE,"E63.trimOffspring")])]});
            var Q11;
            Q11=makeQuery(id+"F3.opExtrude","SWEPT_EDGE",EDGE,{"disambiguationData":[OSD([sQuery(id+"F0.wireOp",EDGE,"E32.top"),sQuery(id+"F0.wireOp",EDGE,"E62.trimOffspring")])]});
            var Q12;
            Q12=makeQuery(id+"F1.opExtrude","SWEPT_EDGE",EDGE,{"disambiguationData":[OSD([sQuery(id+"F0.wireOp",EDGE,"E28.top"),sQuery(id+"F0.wireOp",EDGE,"E28.right")])]});
            fillet(context, id + "F10", {"entities" : qUnion([Q0, Q1, Q2, Q3, Q4, Q5, Q6, Q7, Q8, Q9, Q10, Q11, Q12]), "radius" : 15 * mm, "tangentPropagation" : true, "allowEdgeOverflow" : false});
        }
    });
